# Revit family: Haworth_JiveTable_RoundDiscBase
name_source: partatom
category: Furniture Systems
revit_build: Autodesk Revit 2018 (Build: 20170223_1515(x64)
units: mm (PartAtom-declared; Revit-internal decimal feet)

## family parameters
Always vertical = Yes
Cut with Voids When Loaded = No
OmniClass Number = 23.40.70.14.64.21
OmniClass Title = Systems Furniture
Part Type = Normal
Room Calculation Point = No
Round Connector Dimension = Use Diameter
Shared = No
Work Plane-Based = No

## types (8) — shared parameters
Assembly Code = E2020200
Base Distance = 0"
Custom Size = No
Manufacturer = Haworth, Inc.
Max. Depth Width = 24"
Max. Height = 36"
Min. Depth Width = 12"
Min. Height = 29"
Model = Haworth Jive
One Disk = Yes
Revision Number = 0
Size = Verify Final Dim. w/ Haworth
Standard Depths = 24, 30, 36, 42, 48 in.
Standard Height = 29, 36 in.
Table Thickness = 1 3/16"
Two Disk = No
URL = https://www.haworth.com
URL - Product = https://www.haworth.com
Warranty = http://www.haworth.com

## per-type parameters (varying)
| type | Actual Depth | Actual Height | Actual Table Depth Width | DW | Depth | Description | Disc Distance | Height | Leg Height |
| 24d 24w 29h | 12" | 29" | 24" | 12" | 24" | Haworth Jive Table Round Disc Base - 24d 24w 29h | 8 1/2" | 29" | 27 13/16" |
| 30d 30w 29h | 15" | 29" | 30" | 15" | 30" | Haworth Jive Table Round Disc Base - 30d 30w 29h | 11" | 29" | 27 13/16" |
| 36d 36w 29h | 18" | 29" | 36" | 18" | 36" | Haworth Jive Table Round Disc Base - 36d 36w 29h | 13 1/2" | 29" | 27 13/16" |
| 42d 42w 29h | 21" | 29" | 42" | 21" | 42" | Haworth Jive Table Round Disc Base - 42d 42w 29h | 13 1/2" | 29" | 27 13/16" |
| 30d 30w 36h | 15" | 36" | 30" | 15" | 30" | Haworth Jive Table Round Disc Base - 30d 30w 36h | 11" | 36" | 34 13/16" |
| 36d 36w 36h | 18" | 36" | 36" | 18" | 36" | Haworth Jive Table Round Disc Base - 36d 36w 36h | 13 1/2" | 36" | 34 13/16" |
| 42d 42w 36h | 21" | 36" | 42" | 21" | 42" | Haworth Jive Table Round Disc Base - 42d 42w 36h | 13 1/2" | 36" | 34 13/16" |
| 48d 48w 29h | 24" | 29" | 48" | 24" | 48" | Haworth Jive Table Round Disc Base - 48d 48w 29h | 13 1/2" | 29" | 27 13/16" |

## geometry (parser evidence)
native form markers: Sweep x5
no freeform markers — native parametric forms only
